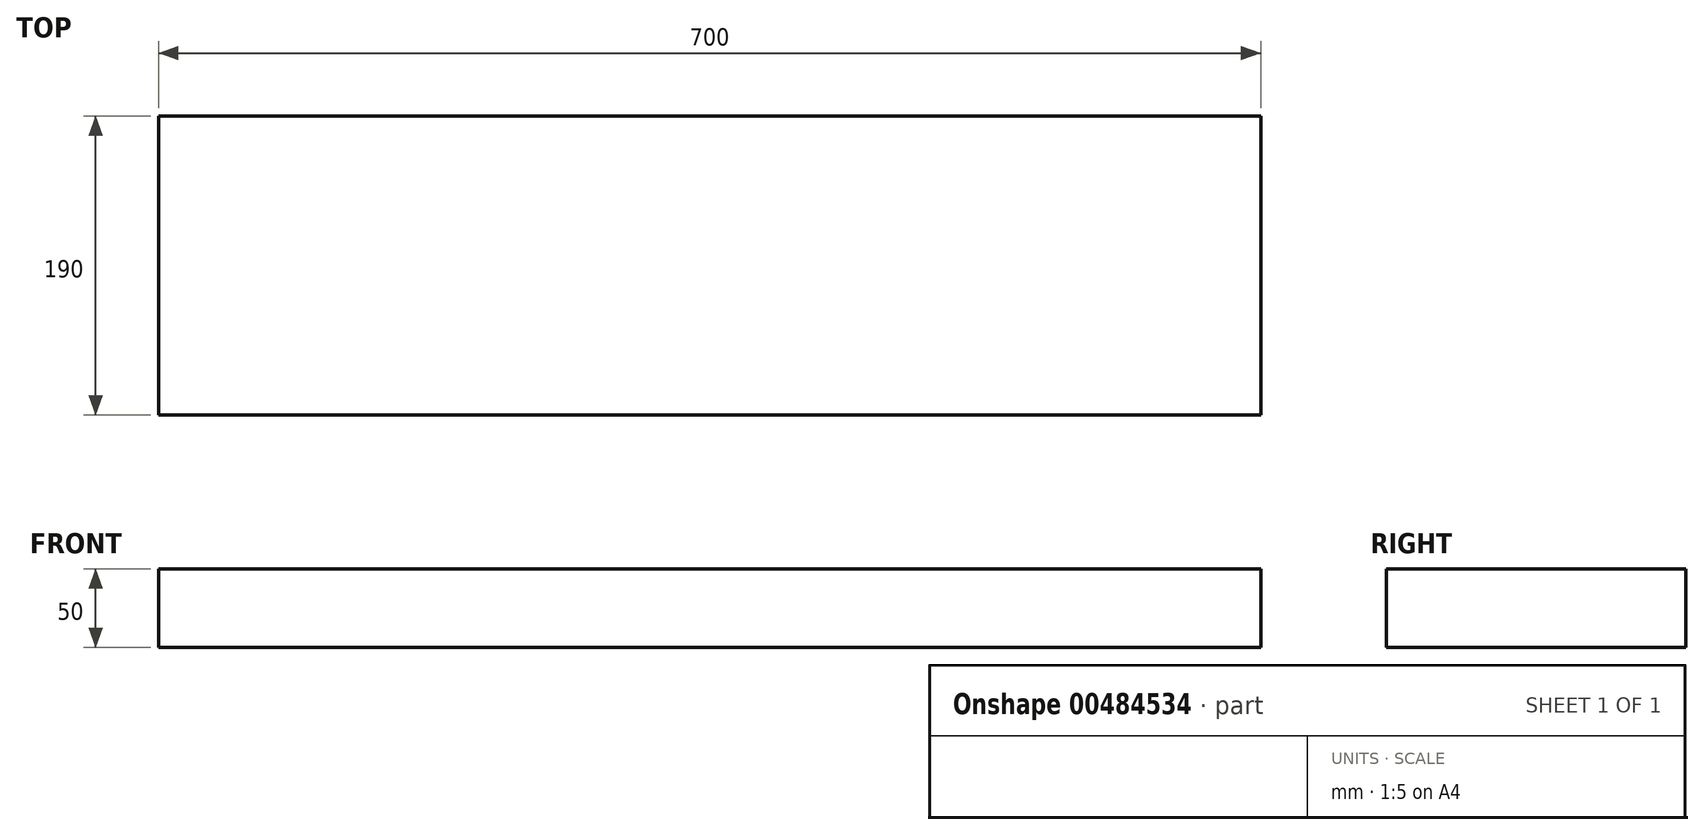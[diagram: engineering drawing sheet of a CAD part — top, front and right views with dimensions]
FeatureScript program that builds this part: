
annotation { "Feature Type Name" : "Feature", "Feature Type Description" : "" }
export const myFeature = defineFeature(function(context is Context, id is Id, definition is map)
    precondition{}
    {
        {
            var Q0;
            Q0=qCreatedBy(makeId("Top.planeOp"),FACE);
            var sketch = newSketch(context, id + "F0", { "sketchPlane" : qUnion([Q0])});
            skLineSegment(sketch, "E0.bottom", {"start": v(-509.87, -280.53) * mm, "end": v(190.13, -280.53) * mm});
            skLineSegment(sketch, "E0.top", {"start": v(-509.87, -90.53) * mm, "end": v(190.13, -90.53) * mm});
            skLineSegment(sketch, "E0.left", {"start": v(-509.87, -280.53) * mm, "end": v(-509.87, -90.53) * mm});
            skLineSegment(sketch, "E0.right", {"start": v(190.13, -280.53) * mm, "end": v(190.13, -90.53) * mm});
            skSolve(sketch);
        }
        {
            var Q0;
            Q0=qSketchRegion(id+"F0",true);
            extrude(context, id + "F1", {"entities" : qUnion([Q0]), "depth" : 50 * mm});
        }
    });
